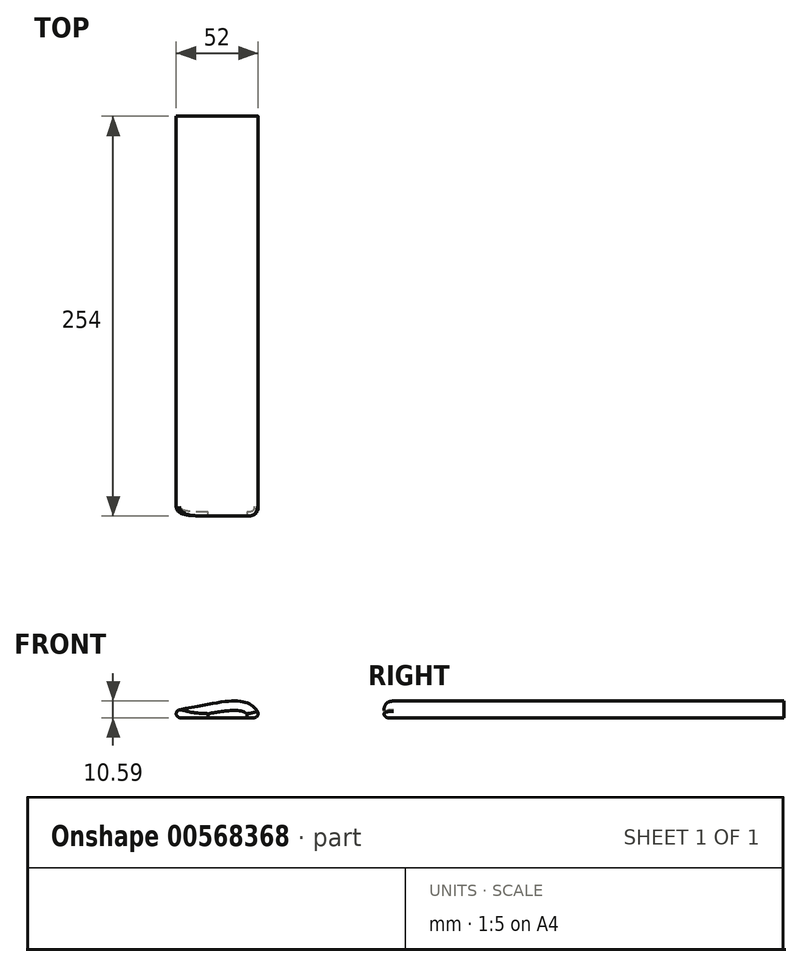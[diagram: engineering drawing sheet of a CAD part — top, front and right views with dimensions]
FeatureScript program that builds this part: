
annotation { "Feature Type Name" : "Feature", "Feature Type Description" : "" }
export const myFeature = defineFeature(function(context is Context, id is Id, definition is map)
    precondition{}
    {
        {
            var Q0;
            Q0=qCreatedBy(makeId("Front.planeOp"),FACE);
            var sketch = newSketch(context, id + "F0", { "sketchPlane" : qUnion([Q0])});
            skLineSegment(sketch, "E0", {"start": v(0, 0) * mm, "end": v(77.38, 0) * mm});
            skFitSpline(sketch, "E1", {"points": [v(0, 0) * mm, v(77.38, 0) * mm], "startDerivative": vector(171.57, 32.07) * mm, "endDerivative": vector(23.82, -51.57) * mm});
            skSolve(sketch);
        }
        {
            var Q0;
            Q0=makeQuery(id+"F0.imprint","IMPRINT",FACE,{"disambiguationData":[TD([[makeQuery(id+"F0.imprint","IMPRINT",EDGE,{"derivedFrom":sQuery(id+"F0.wireOp",EDGE,"E0")}),1.0]])]});
            extrude(context, id + "F1", {"entities" : qUnion([Q0]), "depth" : 254 * mm, "offsetDistance" : 25.4 * mm});
        }
        {
            var Q0;
            Q0=makeQuery(id+"F1.opExtrude","CAP_EDGE",EDGE,{"disambiguationData":[OSD([sQuery(id+"F0.wireOp",EDGE,"E1")])],"isStart":false});
            fillet(context, id + "F2", {"entities" : qUnion([Q0]), "radius" : 5.94 * mm, "tangentPropagation" : true, "rho" : 0.5, "crossSection" : FilletCrossSection.CONIC, "allowEdgeOverflow" : false});
        }
        {
            var Q0;
            Q0=makeQuery(id+"F2.opFillet","BLEND_EDGE",EDGE,{"disambiguationData":[OD(1.0)],"blendedFrom":[makeQuery(id+"F1.opExtrude","CAP_EDGE",EDGE,{"disambiguationData":[OSD([sQuery(id+"F0.wireOp",EDGE,"E1")])],"isStart":false}),makeQuery(id+"F1.opExtrude","SWEPT_FACE",FACE,{"disambiguationData":[OSD([sQuery(id+"F0.wireOp",EDGE,"E0")])]})],"blendedInto":[makeQuery(id+"F1.opExtrude","SWEPT_FACE",FACE,{"disambiguationData":[OSD([sQuery(id+"F0.wireOp",EDGE,"E0")])]})]});
            fillet(context, id + "F3", {"entities" : qUnion([Q0]), "radius" : 2.54 * mm, "tangentPropagation" : true, "allowEdgeOverflow" : false});
        }
    });
